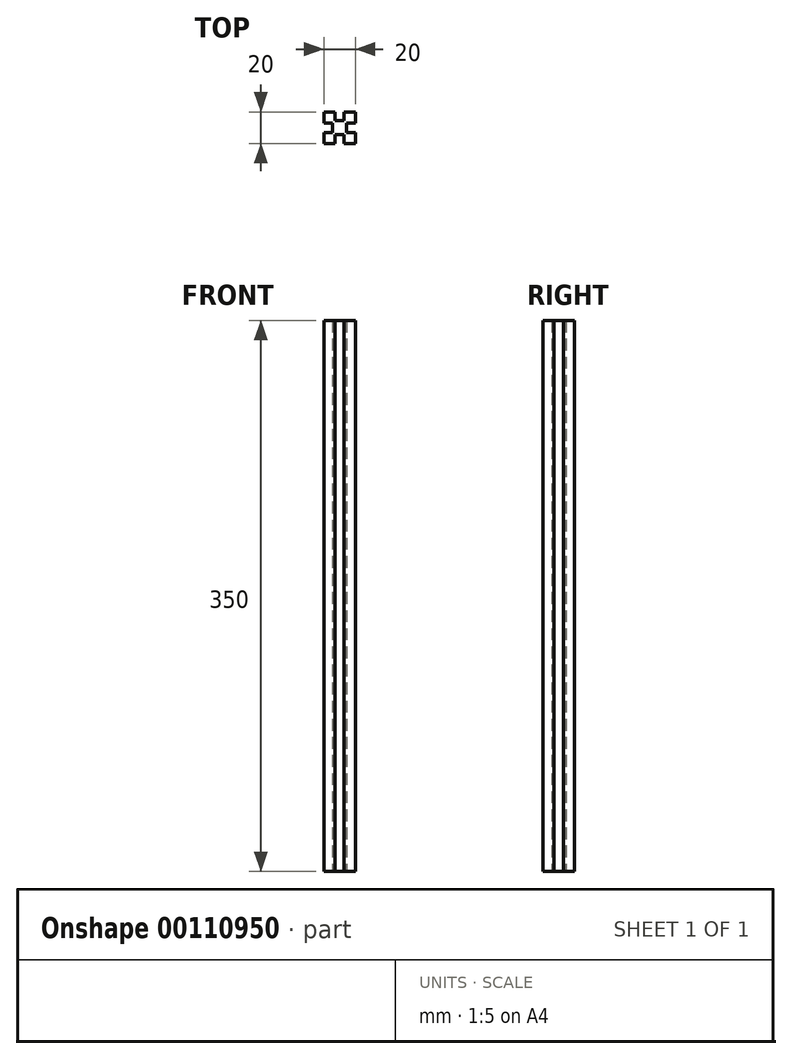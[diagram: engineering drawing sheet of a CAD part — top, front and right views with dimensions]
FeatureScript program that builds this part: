
annotation { "Feature Type Name" : "Feature", "Feature Type Description" : "" }
export const myFeature = defineFeature(function(context is Context, id is Id, definition is map)
    precondition{}
    {
        {
            var Q0;
            Q0=qCreatedBy(makeId("Top.planeOp"),FACE);
            var sketch = newSketch(context, id + "F0", { "sketchPlane" : qUnion([Q0])});
            skLineSegment(sketch, "E0.bottom", {"start": v(0, 0) * mm, "end": v(20, 0) * mm});
            skLineSegment(sketch, "E0.top", {"start": v(0, 20) * mm, "end": v(20, 20) * mm});
            skLineSegment(sketch, "E0.left", {"start": v(0, 0) * mm, "end": v(0, 20) * mm});
            skLineSegment(sketch, "E0.right", {"start": v(20, 0) * mm, "end": v(20, 20) * mm});
            skLineSegment(sketch, "E1.bottom", {"start": v(7, 20) * mm, "end": v(13, 20) * mm});
            skLineSegment(sketch, "E1.top", {"start": v(7, 14.5) * mm, "end": v(13, 14.5) * mm});
            skLineSegment(sketch, "E1.left", {"start": v(7, 20) * mm, "end": v(7, 14.5) * mm});
            skLineSegment(sketch, "E1.right", {"start": v(13, 20) * mm, "end": v(13, 14.5) * mm});
            skLineSegment(sketch, "E2.bottom", {"start": v(20, 13) * mm, "end": v(14.5, 13) * mm});
            skLineSegment(sketch, "E2.top", {"start": v(20, 7) * mm, "end": v(14.5, 7) * mm});
            skLineSegment(sketch, "E2.left", {"start": v(20, 13) * mm, "end": v(20, 7) * mm});
            skLineSegment(sketch, "E2.right", {"start": v(14.5, 13) * mm, "end": v(14.5, 7) * mm});
            skLineSegment(sketch, "E3.bottom", {"start": v(13, 0) * mm, "end": v(7, 0) * mm});
            skLineSegment(sketch, "E3.top", {"start": v(13, 5.5) * mm, "end": v(7, 5.5) * mm});
            skLineSegment(sketch, "E3.left", {"start": v(13, 0) * mm, "end": v(13, 5.5) * mm});
            skLineSegment(sketch, "E3.right", {"start": v(7, 0) * mm, "end": v(7, 5.5) * mm});
            skLineSegment(sketch, "E4.bottom", {"start": v(0, 7) * mm, "end": v(5.5, 7) * mm});
            skLineSegment(sketch, "E4.top", {"start": v(0, 13) * mm, "end": v(5.5, 13) * mm});
            skLineSegment(sketch, "E4.left", {"start": v(0, 7) * mm, "end": v(0, 13) * mm});
            skLineSegment(sketch, "E4.right", {"start": v(5.5, 7) * mm, "end": v(5.5, 13) * mm});
            skSolve(sketch);
        }
        {
            var Q0;
            Q0=makeQuery(id+"F0.imprint","IMPRINT",FACE,{"disambiguationData":[TD([[makeQuery(id+"F0.imprint","IMPRINT",EDGE,{"derivedFrom":sQuery(id+"F0.wireOp",EDGE,"E1.top")}),-1.0]])]});
            extrude(context, id + "F1", {"entities" : qUnion([Q0]), "depth" : 350 * mm});
        }
        {
            var Q0;
            {var subQ0=sQuery(id+"F0.wireOp",EDGE,"E0.bottom");Q0=makeQuery(id+"F1.opExtrude","SWEPT_FACE",FACE,{"disambiguationData":[OSD([subQ0]),TDD([makeQuery(id+"F0.imprint","IMPRINT",EDGE,{"disambiguationData":[TD([[makeQuery(id+"F0.imprint","INTERSECT",VERTEX,{"derivedFrom":[subQ0,sQuery(id+"F0.wireOp",EDGE,"E0.left")]}),-1.0]])],"derivedFrom":subQ0})])]});}
            var sketch = newSketch(context, id + "F2", { "sketchPlane" : qUnion([Q0])});
            skCircle(sketch, "E5", {"center": v(10, 336.5) * mm, "radius": 7.5 * mm});
            skCircle(sketch, "E6", {"center": v(10, 13.5) * mm, "radius": 7.5 * mm});
            skCircle(sketch, "E7", {"center": v(10, 318.5) * mm, "radius": 2 * mm});
            skCircle(sketch, "E8", {"center": v(10, 31.5) * mm, "radius": 2 * mm});
            skLineSegment(sketch, "E9", {"start": v(10, 318.5) * mm, "end": v(10, 329) * mm});
            skLineSegment(sketch, "E10", {"start": v(10, 31.5) * mm, "end": v(10, 21) * mm});
            skSolve(sketch);
        }
    });
